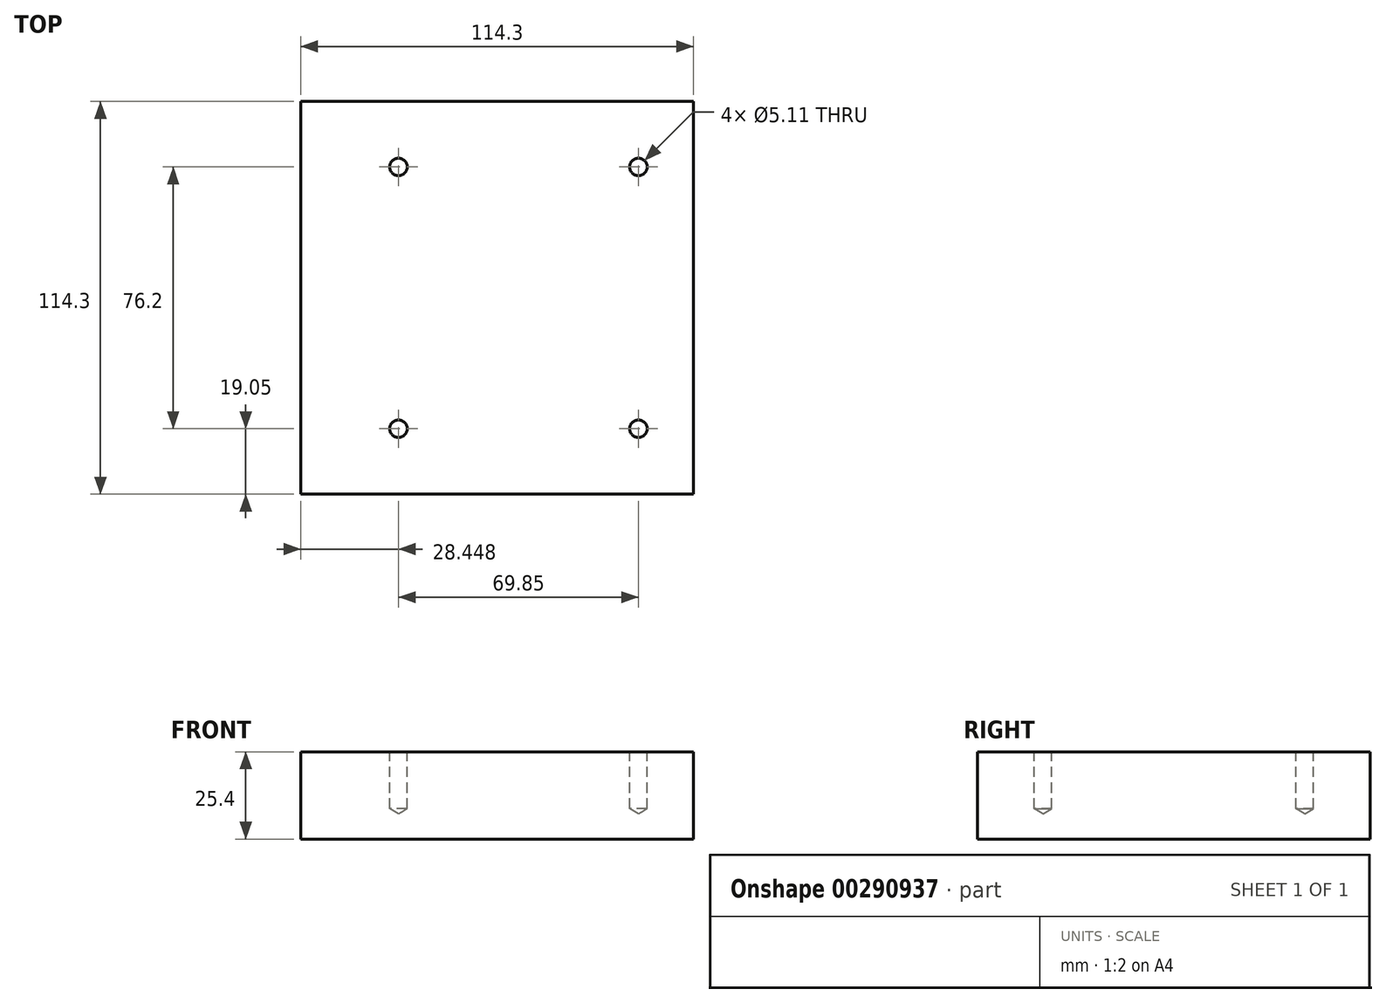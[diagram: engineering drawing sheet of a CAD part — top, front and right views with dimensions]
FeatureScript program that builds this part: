
annotation { "Feature Type Name" : "Feature", "Feature Type Description" : "" }
export const myFeature = defineFeature(function(context is Context, id is Id, definition is map)
    precondition{}
    {
        {
            var Q0;
            Q0=qCreatedBy(makeId("Top.planeOp"),FACE);
            var sketch = newSketch(context, id + "F0", { "sketchPlane" : qUnion([Q0])});
            skLineSegment(sketch, "E0.bottom", {"start": v(-57.15, 57.15) * mm, "end": v(57.15, 57.15) * mm});
            skLineSegment(sketch, "E0.top", {"start": v(-57.15, -57.15) * mm, "end": v(57.15, -57.15) * mm});
            skLineSegment(sketch, "E0.left", {"start": v(-57.15, 57.15) * mm, "end": v(-57.15, -57.15) * mm});
            skLineSegment(sketch, "E0.right", {"start": v(57.15, 57.15) * mm, "end": v(57.15, -57.15) * mm});
            skPoint(sketch, "E0.middle", {"position": v(0, 0) * mm});
            skSolve(sketch);
        }
        {
            var Q0;
            Q0 = qSketchRegion(id + "F0", true);
            extrude(context, id + "F1", {"entities" : qUnion([Q0]), "depth" : 25.4 * mm});
        }
        {
            var Q0;
            Q0=makeQuery(id+"F1.opExtrude","CAP_FACE",FACE,{"disambiguationData":[OSD([sQuery(id+"F0.wireOp",EDGE,"E0.bottom"),sQuery(id+"F0.wireOp",EDGE,"E0.top"),sQuery(id+"F0.wireOp",EDGE,"E0.left"),sQuery(id+"F0.wireOp",EDGE,"E0.right")])],"isStart":false});
            var sketch = newSketch(context, id + "F2", { "sketchPlane" : qUnion([Q0])});
            skLineSegment(sketch, "E1.0", {"start": v(-57.15, 57.15) * mm, "end": v(-57.15, -57.15) * mm, "construction": true});
            skLineSegment(sketch, "E2", {"start": v(-100.83, 0) * mm, "end": v(119.32, 0) * mm, "construction": true});
            skPoint(sketch, "E2.startSnap0", {"position": v(-57.15, 0) * mm});
            skPoint(sketch, "E2.endSnap0", {"position": v(-57.15, 0) * mm});
            skLineSegment(sketch, "E3.0", {"start": v(-28.7, 57.15) * mm, "end": v(-28.7, -57.15) * mm, "construction": true});
            skLineSegment(sketch, "E4.0", {"start": v(41.15, 57.15) * mm, "end": v(41.15, -57.15) * mm, "construction": true});
            skLineSegment(sketch, "E5.0", {"start": v(-100.83, -38.1) * mm, "end": v(119.32, -38.1) * mm, "construction": true});
            skPoint(sketch, "E6", {"position": v(-28.7, -38.1) * mm});
            skPoint(sketch, "E7", {"position": v(41.15, -38.1) * mm});
            skPoint(sketch, "E8.MirrorP", {"position": v(-28.7, 38.1) * mm});
            skPoint(sketch, "E9.MirrorP", {"position": v(41.15, 38.1) * mm});
            skSolve(sketch);
        }
        {
            var Q0;
            Q0=sQuery(id+"F2.wireOp",VERTEX,"E8.MirrorP");
            var Q1;
            Q1=sQuery(id+"F2.wireOp",VERTEX,"E9.MirrorP");
            var Q2;
            Q2=sQuery(id+"F2.wireOp",VERTEX,"E6");
            var Q3;
            Q3=sQuery(id+"F2.wireOp",VERTEX,"E7");
            var Q4;
            Q4=makeQuery(id+"F1.opExtrude","SWEPT_BODY",BODY,{"disambiguationData":[OSD([sQuery(id+"F0.wireOp",EDGE,"E0.bottom"),sQuery(id+"F0.wireOp",EDGE,"E0.top"),sQuery(id+"F0.wireOp",EDGE,"E0.left"),sQuery(id+"F0.wireOp",EDGE,"E0.right")])]});
            hole(context, id + "F3", {"style" : HoleStyle.SIMPLE, "endStyle" : HoleEndStyle.BLIND, "standardTappedOrClearance" : lookupTablePath({ "standard" : "ANSI", "engagement" : "75%", "pitch" : "20 tpi", "size" : "1/4", "type" : "Tapped" }), "standardBlindInLast" : lookupTablePath({ "standard" : "ANSI", "engagement" : "75%", "pitch" : "20 tpi", "size" : "1/4", "type" : "Tapped" }), "holeDiameter" : 5.1 * mm, "showTappedDepth" : true, "holeDepth" : 16.51 * mm, "tappedDepth" : 12.7 * mm, "tapClearance" : 3, "locations" : qUnion([Q0, Q1, Q2, Q3]), "scope" : qUnion([Q4]), "majorDiameter" : 6.35 * mm});
        }
    });
